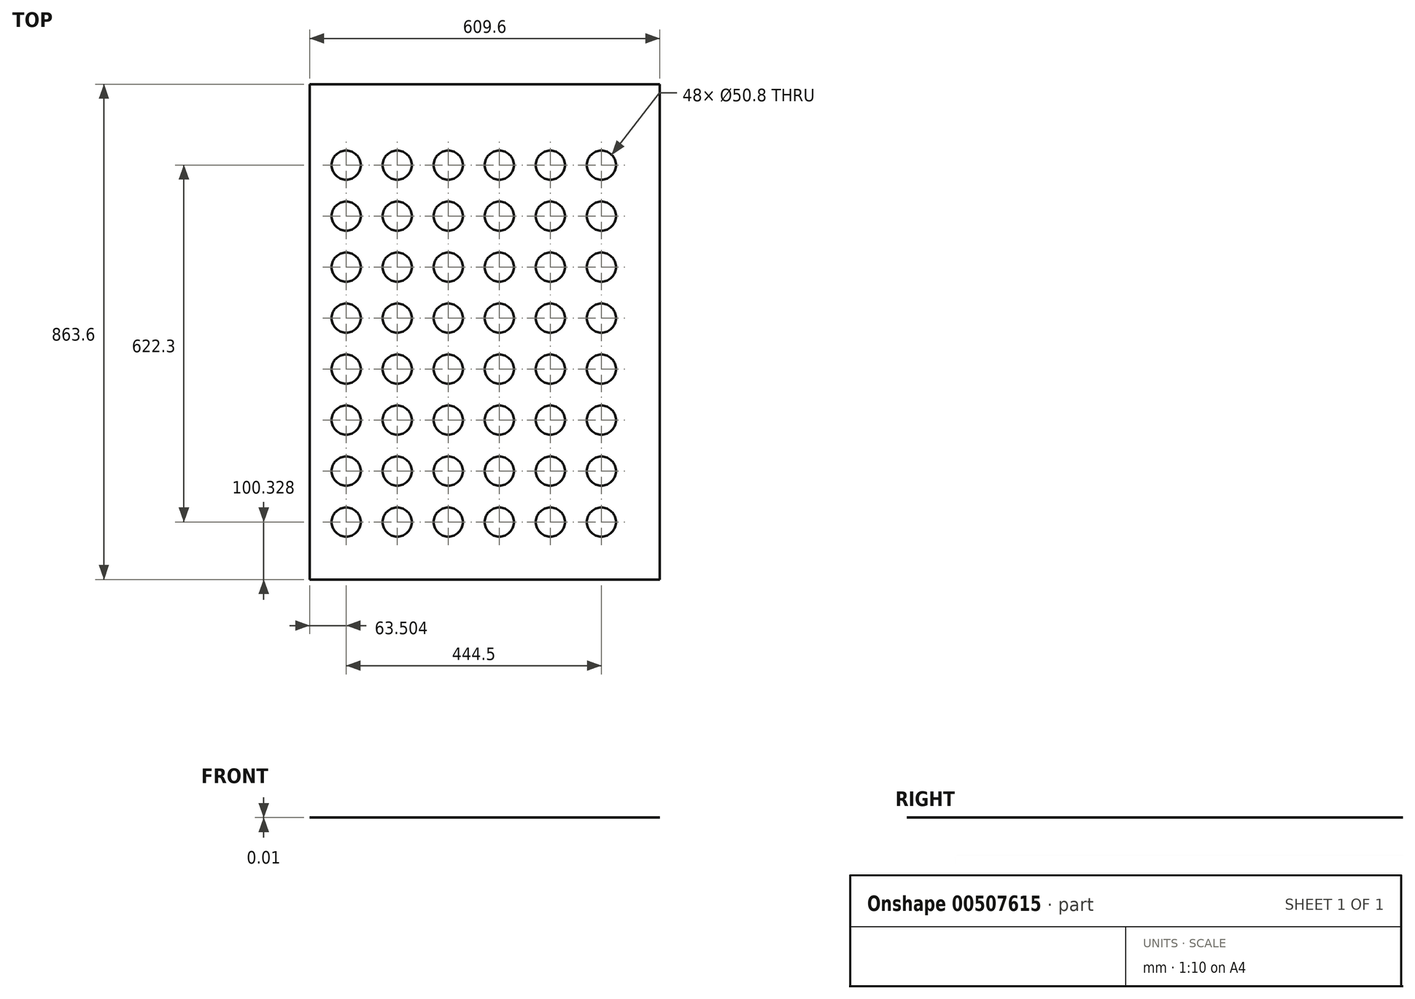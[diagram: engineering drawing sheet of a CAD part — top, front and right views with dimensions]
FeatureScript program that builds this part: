
annotation { "Feature Type Name" : "Feature", "Feature Type Description" : "" }
export const myFeature = defineFeature(function(context is Context, id is Id, definition is map)
    precondition{}
    {
        {
            var Q0;
            Q0=qCreatedBy(makeId("Top.planeOp"),FACE);
            var sketch = newSketch(context, id + "F0", { "sketchPlane" : qUnion([Q0])});
            skLineSegment(sketch, "E0.bottom", {"start": v(-546.36, 786.78) * mm, "end": v(63.24, 786.78) * mm});
            skLineSegment(sketch, "E0.top", {"start": v(-546.36, -76.82) * mm, "end": v(63.24, -76.82) * mm});
            skLineSegment(sketch, "E0.left", {"start": v(-546.36, 786.78) * mm, "end": v(-546.36, -76.82) * mm});
            skLineSegment(sketch, "E0.right", {"start": v(63.24, 786.78) * mm, "end": v(63.24, -76.82) * mm});
            skCircle(sketch, "E1", {"center": v(-482.86, 645.8) * mm, "radius": 25.4 * mm});
            skCircle(sketch, "E2.0.1.0", {"center": v(-482.86, 556.9) * mm, "radius": 25.4 * mm});
            skCircle(sketch, "E2.0.2.0", {"center": v(-482.86, 468) * mm, "radius": 25.4 * mm});
            skCircle(sketch, "E2.0.3.0", {"center": v(-482.86, 379.1) * mm, "radius": 25.4 * mm});
            skCircle(sketch, "E2.0.4.0", {"center": v(-482.86, 290.2) * mm, "radius": 25.4 * mm});
            skCircle(sketch, "E2.0.5.0", {"center": v(-482.86, 201.3) * mm, "radius": 25.4 * mm});
            skCircle(sketch, "E2.0.6.0", {"center": v(-482.86, 112.4) * mm, "radius": 25.4 * mm});
            skCircle(sketch, "E2.0.7.0", {"center": v(-482.86, 23.5) * mm, "radius": 25.4 * mm});
            skCircle(sketch, "E2.1.0.0", {"center": v(-393.96, 645.8) * mm, "radius": 25.4 * mm});
            skCircle(sketch, "E2.1.1.0", {"center": v(-393.96, 556.9) * mm, "radius": 25.4 * mm});
            skCircle(sketch, "E2.1.2.0", {"center": v(-393.96, 468) * mm, "radius": 25.4 * mm});
            skCircle(sketch, "E2.1.3.0", {"center": v(-393.96, 379.1) * mm, "radius": 25.4 * mm});
            skCircle(sketch, "E2.1.4.0", {"center": v(-393.96, 290.2) * mm, "radius": 25.4 * mm});
            skCircle(sketch, "E2.1.5.0", {"center": v(-393.96, 201.3) * mm, "radius": 25.4 * mm});
            skCircle(sketch, "E2.1.6.0", {"center": v(-393.96, 112.4) * mm, "radius": 25.4 * mm});
            skCircle(sketch, "E2.1.7.0", {"center": v(-393.96, 23.5) * mm, "radius": 25.4 * mm});
            skCircle(sketch, "E2.2.0.0", {"center": v(-305.06, 645.8) * mm, "radius": 25.4 * mm});
            skCircle(sketch, "E2.2.1.0", {"center": v(-305.06, 556.9) * mm, "radius": 25.4 * mm});
            skCircle(sketch, "E2.2.2.0", {"center": v(-305.06, 468) * mm, "radius": 25.4 * mm});
            skCircle(sketch, "E2.2.3.0", {"center": v(-305.06, 379.1) * mm, "radius": 25.4 * mm});
            skCircle(sketch, "E2.2.4.0", {"center": v(-305.06, 290.2) * mm, "radius": 25.4 * mm});
            skCircle(sketch, "E2.2.5.0", {"center": v(-305.06, 201.3) * mm, "radius": 25.4 * mm});
            skCircle(sketch, "E2.2.6.0", {"center": v(-305.06, 112.4) * mm, "radius": 25.4 * mm});
            skCircle(sketch, "E2.2.7.0", {"center": v(-305.06, 23.5) * mm, "radius": 25.4 * mm});
            skCircle(sketch, "E2.3.0.0", {"center": v(-216.16, 645.8) * mm, "radius": 25.4 * mm});
            skCircle(sketch, "E2.3.1.0", {"center": v(-216.16, 556.9) * mm, "radius": 25.4 * mm});
            skCircle(sketch, "E2.3.2.0", {"center": v(-216.16, 468) * mm, "radius": 25.4 * mm});
            skCircle(sketch, "E2.3.3.0", {"center": v(-216.16, 379.1) * mm, "radius": 25.4 * mm});
            skCircle(sketch, "E2.3.4.0", {"center": v(-216.16, 290.2) * mm, "radius": 25.4 * mm});
            skCircle(sketch, "E2.3.5.0", {"center": v(-216.16, 201.3) * mm, "radius": 25.4 * mm});
            skCircle(sketch, "E2.3.6.0", {"center": v(-216.16, 112.4) * mm, "radius": 25.4 * mm});
            skCircle(sketch, "E2.3.7.0", {"center": v(-216.16, 23.5) * mm, "radius": 25.4 * mm});
            skCircle(sketch, "E2.4.0.0", {"center": v(-127.26, 645.8) * mm, "radius": 25.4 * mm});
            skCircle(sketch, "E2.4.1.0", {"center": v(-127.26, 556.9) * mm, "radius": 25.4 * mm});
            skCircle(sketch, "E2.4.2.0", {"center": v(-127.26, 468) * mm, "radius": 25.4 * mm});
            skCircle(sketch, "E2.4.3.0", {"center": v(-127.26, 379.1) * mm, "radius": 25.4 * mm});
            skCircle(sketch, "E2.4.4.0", {"center": v(-127.26, 290.2) * mm, "radius": 25.4 * mm});
            skCircle(sketch, "E2.4.5.0", {"center": v(-127.26, 201.3) * mm, "radius": 25.4 * mm});
            skCircle(sketch, "E2.4.6.0", {"center": v(-127.26, 112.4) * mm, "radius": 25.4 * mm});
            skCircle(sketch, "E2.4.7.0", {"center": v(-127.26, 23.5) * mm, "radius": 25.4 * mm});
            skCircle(sketch, "E2.5.0.0", {"center": v(-38.36, 645.8) * mm, "radius": 25.4 * mm});
            skCircle(sketch, "E2.5.1.0", {"center": v(-38.36, 556.9) * mm, "radius": 25.4 * mm});
            skCircle(sketch, "E2.5.2.0", {"center": v(-38.36, 468) * mm, "radius": 25.4 * mm});
            skCircle(sketch, "E2.5.3.0", {"center": v(-38.36, 379.1) * mm, "radius": 25.4 * mm});
            skCircle(sketch, "E2.5.4.0", {"center": v(-38.36, 290.2) * mm, "radius": 25.4 * mm});
            skCircle(sketch, "E2.5.5.0", {"center": v(-38.36, 201.3) * mm, "radius": 25.4 * mm});
            skCircle(sketch, "E2.5.6.0", {"center": v(-38.36, 112.4) * mm, "radius": 25.4 * mm});
            skCircle(sketch, "E2.5.7.0", {"center": v(-38.36, 23.5) * mm, "radius": 25.4 * mm});
            skLineSegment(sketch, "E2.direction1", {"start": v(-482.86, 645.8) * mm, "end": v(-393.96, 645.8) * mm, "construction": true});
            skLineSegment(sketch, "E2.direction2", {"start": v(-482.86, 645.8) * mm, "end": v(-482.86, 556.9) * mm, "construction": true});
            skSolve(sketch);
        }
        {
            var Q0;
            Q0 = qSketchRegion(id + "F0", true);
            extrude(context, id + "F1", {"entities" : qUnion([Q0]), "depth" : 3 / 406.4 * mm, "offsetDistance" : 25.4 * mm});
        }
    });
